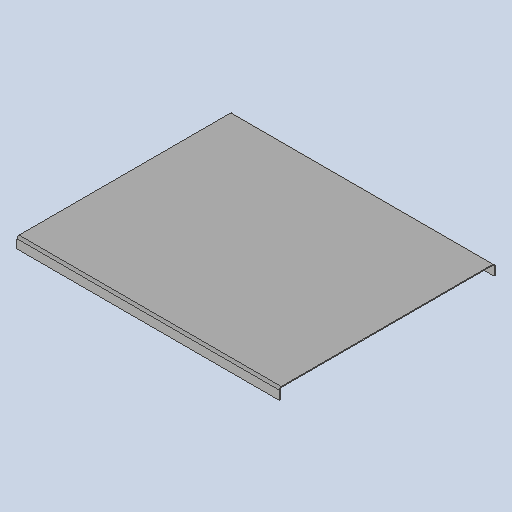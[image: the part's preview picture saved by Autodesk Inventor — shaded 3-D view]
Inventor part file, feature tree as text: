
AUTODESK INVENTOR PART (.ipt)
format: ipt  version: 2025 (Build 290162010, 162A)  size: 299,008 bytes
history: native  units: mm
features: other x5, sheet_metal_op x4, sketch x3
ambient origin geometry x8: Origin, YZ Plane, XZ Plane, XY Plane, X Axis, Y Axis, Z Axis, Center Point
bodies: Solid1 (feature_tree)
feature tree (12):
  sheet_metal_op  "Face1"
  other  "Mark1"
  other  "A-Side Definition"
  sheet_metal_op  "Flange1"
  sketch  "Sketch1"  dims[d0=600.0mm]
  other  "Plate1"
  sketch  "Sketch2"  dims[d1=490.0mm]
  sketch  "Sketch3"  dims[d2=2.0mm d6=200.0mm d9=20.0mm d10=20.0mm d11=20.0mm d12=2.0mm d13=1.0mm d14=4.0mm d15=2.75mm d16=25.0mm d17=90.0deg d18=2.75mm d19=8.0mm d20=2.0mm d21=2.75mm]
  other  "Plate2"
  sheet_metal_op  "Bend1"
  sheet_metal_op  "Corner1"
  other  "Definition1"
